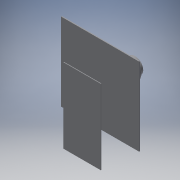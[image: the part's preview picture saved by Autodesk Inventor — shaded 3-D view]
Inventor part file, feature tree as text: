
AUTODESK INVENTOR PART (.ipt)
format: ipt  version: 2019 (Build 230136000, 136)  size: 216,064 bytes
history: native  units: mm
features: sketch x11, extrude x7, plane x6, hole x1
ambient origin geometry x8: Origin, YZ Plane, XZ Plane, XY Plane, X Axis, Y Axis, Z Axis, Center Point
bodies: Solid1 (feature_tree)
feature tree (25):
  extrude  "Extrusion1"  Depth=30.0mm TaperAngle=0.0deg
  extrude  "Extrusion2"  Depth=125.0mm TaperAngle=0.0deg
  extrude  "Extrusion3"  Depth=920.0mm
  sketch  "Sketch5"  dims[d9=1250.0mm d10=900.0mm]
  plane  "Work Plane1"
  sketch  "Sketch7"  dims[d11=1250.0mm d12=15.0mm d13=0.0mm]
  plane  "Work Plane2"
  sketch  "Sketch8"  dims[d14=885.0mm d15=335.0mm]
  plane  "Work Plane3"
  sketch  "Sketch9"  dims[d16=315.0mm d17=905.0mm]
  plane  "Work Plane4"
  sketch  "Sketch10"  dims[d18=370.0mm d19=315.0mm]
  plane  "Work Plane5"
  sketch  "Sketch11"  dims[d20=440.0mm]
  hole  "Hole1"  [1 undecoded]
  plane  "Work Plane8"
  extrude  "Extrusion4"  Depth=15.0mm TaperAngle=0.0deg
  extrude  "Extrusion5"  Depth=335.0mm
  extrude  "Extrusion6"  Depth=905.0mm
  extrude  "Extrusion7"  Depth=315.0mm
  sketch  "Sketch1"  dims[d0=261.0mm d1=30.0mm d2=0.0mm]
  sketch  "Sketch2"  dims[d3=345.0mm d4=125.0mm d5=0.0mm]
  sketch  "Sketch3"  dims[d6=95.0mm d7=0.0mm d8=920.0mm]
  sketch  "Sketch13"  dims[d22=335.0mm]
  sketch  "Sketch14"  dims[d23=-25.0mm d24=25.0mm d25=35.0mm d26=1200.0mm d27=970.0mm d28=-25.0mm d29=25.0mm d30=35.0mm d31=1200.0mm d32=970.0mm d33=600.0mm d34=-25.0mm d35=25.0mm d36=35.0mm d37=1200.0mm d38=970.0mm d39=600.0mm d40=-25.0mm d41=25.0mm d42=35.0mm d43=1200.0mm d44=970.0mm d45=600.0mm d46=585.0mm d47=25.0mm d48=25.0mm d49=1200.0mm d50=625.0mm d53=30.0mm d54=28.0mm d55=4.0mm d56=2.0mm d57=90.0deg d58=190.0mm d59=27.925268mm d60=30.0mm d61=90.0mm d62=105.0mm d63=0.0mm d64=52.75mm d65=0.0mm d66=0.0mm d67=250.0mm d68=250.0mm d69=250.0mm d70=250.0mm d71=250.0mm d72=250.0mm d73=10.0mm d74=0.0mm d75=10.0mm d76=0.0mm d78=600.0mm d79=600.0mm d80=600.0mm d81=10.0mm d82=0.0mm]
note: 1 required parameter value undecoded (feature->parameter linkage not recoverable at this tier; creation-order binding heuristic only, values carry confidence <= 0.55)
